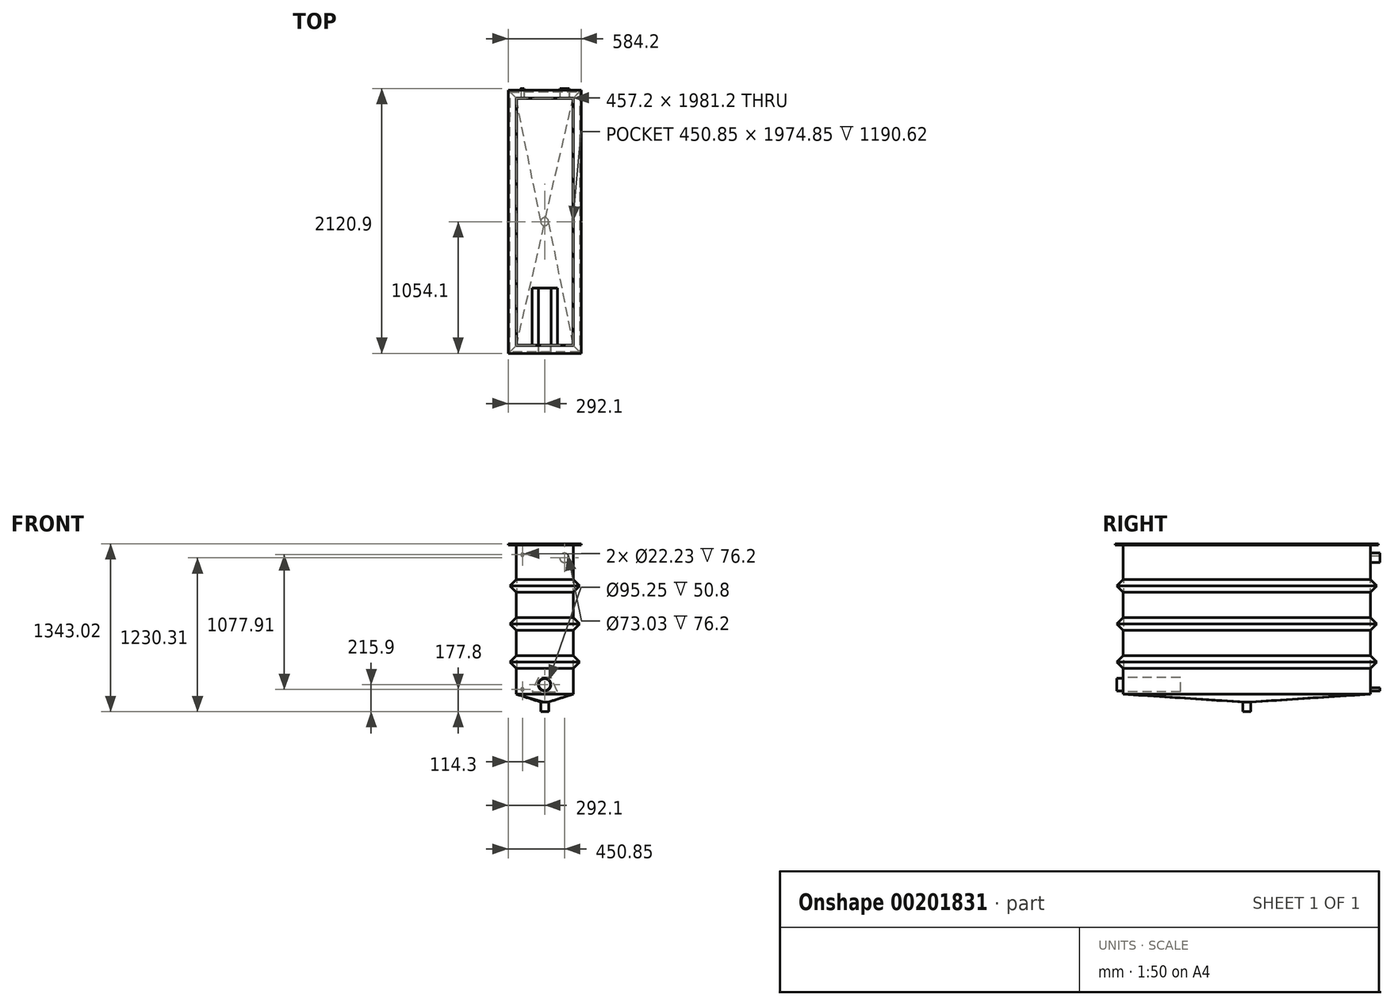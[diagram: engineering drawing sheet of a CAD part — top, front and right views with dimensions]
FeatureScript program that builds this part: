
annotation { "Feature Type Name" : "Feature", "Feature Type Description" : "" }
export const myFeature = defineFeature(function(context is Context, id is Id, definition is map)
    precondition{}
    {
        {
            var Q0;
            Q0=qCreatedBy(makeId("Right.planeOp"),FACE);
            var sketch = newSketch(context, id + "F0", { "sketchPlane" : qUnion([Q0])});
            skLineSegment(sketch, "E0.bottom", {"start": v(-990.6, 596.9) * mm, "end": v(990.6, 596.9) * mm});
            skLineSegment(sketch, "E0.top", {"start": v(-990.6, -596.9) * mm, "end": v(990.6, -596.9) * mm});
            skLineSegment(sketch, "E0.left", {"start": v(-990.6, 596.9) * mm, "end": v(-990.6, -596.9) * mm});
            skLineSegment(sketch, "E0.right", {"start": v(990.6, 596.9) * mm, "end": v(990.6, -596.9) * mm});
            skSolve(sketch);
        }
        {
            var Q0;
            Q0=makeQuery(id+"F0.imprint","IMPRINT",FACE,{"disambiguationData":[TD([[makeQuery(id+"F0.imprint","IMPRINT",EDGE,{"derivedFrom":sQuery(id+"F0.wireOp",EDGE,"E0.bottom")}),-1.0]])]});
            extrude(context, id + "F1", {"entities" : qUnion([Q0]), "endBound" : BoundingType.SYMMETRIC, "depth" : 457.2 * mm, "hasSecondDirection" : true, "secondDirectionOppositeDirection" : true, "secondDirectionDepth" : 228.6 * mm});
        }
        {
            var Q0;
            Q0=makeQuery(id+"F1.opExtrude","SWEPT_FACE",FACE,{"disambiguationData":[OSD([sQuery(id+"F0.wireOp",EDGE,"E0.bottom")])]});
            shell(context, id + "F2", {"entities" : qUnion([Q0]), "thickness" : 3.17 * mm});
        }
        {
            var Q0;
            Q0=makeQuery(id+"F1.opExtrude","SWEPT_FACE",FACE,{"disambiguationData":[OSD([sQuery(id+"F0.wireOp",EDGE,"E0.left")])]});
            var sketch = newSketch(context, id + "F3", { "sketchPlane" : qUnion([Q0])});
            skCircle(sketch, "E1", {"center": v(0, -520.7) * mm, "radius": 50.8 * mm});
            skCircle(sketch, "E2", {"center": v(0, -520.7) * mm, "radius": 47.63 * mm});
            skLineSegment(sketch, "E3", {"start": v(-571.69, -393.7) * mm, "end": v(666.68, -393.7) * mm, "construction": true});
            skSolve(sketch);
        }
        {
            var Q0;
            Q0=qSketchRegion(id+"F3",true);
            extrude(context, id + "F4", {"entities" : qUnion([Q0]), "depth" : 50.8 * mm});
        }
        {
            var Q0;
            Q0=makeQuery(id+"F2.opShell","OFFSET_FACE",FACE,{"disambiguationData":[OSD([sQuery(id+"F0.wireOp",EDGE,"E0.left")])]});
            var sketch = newSketch(context, id + "F5", { "sketchPlane" : qUnion([Q0])});
            skPoint(sketch, "E4", {"position": v(0, -520.7) * mm});
            skCircle(sketch, "E5", {"center": v(0, -520.7) * mm, "radius": 38.1 * mm, "construction": true});
            skLineSegment(sketch, "E6", {"start": v(-101.6, -577.85) * mm, "end": v(-50.8, -463.55) * mm});
            skLineSegment(sketch, "E7", {"start": v(-50.8, -463.55) * mm, "end": v(50.8, -463.55) * mm});
            skLineSegment(sketch, "E8", {"start": v(50.8, -463.55) * mm, "end": v(101.6, -577.85) * mm});
            skLineSegment(sketch, "E9", {"start": v(101.6, -577.85) * mm, "end": v(-101.6, -577.85) * mm});
            skSolve(sketch);
        }
        {
            var Q0;
            Q0=makeQuery(id+"F5.imprint","IMPRINT",FACE,{"disambiguationData":[TD([[makeQuery(id+"F5.imprint","IMPRINT",EDGE,{"derivedFrom":sQuery(id+"F5.wireOp",EDGE,"E6")}),-1.0]])]});
            extrude(context, id + "F6", {"entities" : qUnion([Q0]), "operationType" : NewBodyOperationType.ADD, "depth" : 457.2 * mm});
        }
        {
            var Q0;
            {var subQ1=sQuery(id+"F0.wireOp",EDGE,"E0.right");var subQ3=sQuery(id+"F0.wireOp",EDGE,"E0.bottom");Q0=makeQuery(id+"FLVfAFfTKYoEC7O_3.boolean.opBoolean","SPLIT",FACE,{"disambiguationData":[TD([makeQuery(id+"F1.opExtrude","SWEPT_FACE",FACE,{"disambiguationData":[OSD([subQ3])]})])],"derivedFrom":makeQuery(id+"F1.opExtrude","SWEPT_FACE",FACE,{"disambiguationData":[OSD([subQ1])]})});}
            var sketch = newSketch(context, id + "F7", { "sketchPlane" : qUnion([Q0])});
            skPoint(sketch, "E10", {"position": v(-158.75, 493.71) * mm});
            skCircle(sketch, "E11", {"center": v(-158.75, 493.71) * mm, "radius": 38.1 * mm});
            skCircle(sketch, "E12", {"center": v(-158.75, 493.71) * mm, "radius": 36.51 * mm});
            skPoint(sketch, "E13", {"position": v(-158.75, 457.2) * mm});
            skCircle(sketch, "E14", {"center": v(177.8, 519.11) * mm, "radius": 12.7 * mm});
            skCircle(sketch, "E15", {"center": v(177.8, 519.11) * mm, "radius": 11.11 * mm});
            skCircle(sketch, "E16", {"center": v(177.8, -558.8) * mm, "radius": 12.7 * mm});
            skCircle(sketch, "E17", {"center": v(177.8, -558.8) * mm, "radius": 11.11 * mm});
            skLineSegment(sketch, "E18", {"start": v(-180.53, -571.5) * mm, "end": v(332.18, -571.5) * mm, "construction": true});
            skLineSegment(sketch, "E19", {"start": v(-158.75, 493.71) * mm, "end": v(-158.75, 368.33) * mm, "construction": true});
            skPoint(sketch, "E20", {"position": v(-228.6, -381) * mm});
            skLineSegment(sketch, "E21", {"start": v(-172.42, 531.81) * mm, "end": v(289.09, 531.81) * mm, "construction": true});
            skSolve(sketch);
        }
        {
            var Q0;
            Q0=qSketchRegion(id+"F7",true);
            extrude(context, id + "F8", {"entities" : qUnion([Q0]), "operationType" : NewBodyOperationType.ADD, "depth" : 76.2 * mm});
        }
        {
            var Q0;
            Q0=makeQuery(id+"F2.opShell","OFFSET_FACE",FACE,{"disambiguationData":[OSD([sQuery(id+"F0.wireOp",EDGE,"E0.top")])]});
            cPlane(context, id + "F9", {"entities" : qUnion([Q0]), "cplaneType" : CPlaneType.OFFSET, "offset" : 254 * mm, "width" : 152.4 * mm, "height" : 152.4 * mm});
        }
        {
            var Q0;
            Q0=qCreatedBy(id+"F9.planeOp",FACE);
            var sketch = newSketch(context, id + "F10", { "sketchPlane" : qUnion([Q0])});
            skPoint(sketch, "E22", {"position": v(-225.43, 987.43) * mm});
            skPoint(sketch, "E23", {"position": v(228.6, 990.6) * mm});
            skPoint(sketch, "E24", {"position": v(228.6, -990.6) * mm});
            skPoint(sketch, "E25", {"position": v(-228.6, -990.6) * mm});
            skLineSegment(sketch, "E26", {"start": v(-228.6, -990.6) * mm, "end": v(-225.42, 987.43) * mm});
            skLineSegment(sketch, "E27", {"start": v(228.6, 990.6) * mm, "end": v(228.6, -990.6) * mm});
            skLineSegment(sketch, "E28", {"start": v(-225.42, 987.43) * mm, "end": v(228.6, 990.6) * mm});
            skLineSegment(sketch, "E29", {"start": v(-228.6, -990.6) * mm, "end": v(228.6, -990.6) * mm});
            skSolve(sketch);
        }
        {
            var Q0;
            Q0=makeQuery(id+"F1.opExtrude","SWEPT_FACE",FACE,{"disambiguationData":[OSD([sQuery(id+"F0.wireOp",EDGE,"E0.left")])]});
            var sketch = newSketch(context, id + "F11", { "sketchPlane" : qUnion([Q0])});
            skLineSegment(sketch, "E30", {"start": v(-228.6, -339.72) * mm, "end": v(-228.6, -390.52) * mm});
            skLineSegment(sketch, "E31", {"start": v(-228.6, -390.52) * mm, "end": v(-279.4, -339.72) * mm});
            skLineSegment(sketch, "E32", {"start": v(-279.4, -339.72) * mm, "end": v(-228.6, -288.92) * mm});
            skLineSegment(sketch, "E33", {"start": v(-228.6, -288.92) * mm, "end": v(-228.6, -339.72) * mm});
            skSolve(sketch);
        }
        {
            var Q0;
            Q0=makeQuery(id+"F11.imprint","IMPRINT",FACE,{"disambiguationData":[TD([[makeQuery(id+"F11.imprint","IMPRINT",EDGE,{"derivedFrom":sQuery(id+"F11.wireOp",EDGE,"E30")}),-1.0]])]});
            var Q1;
            Q1=sQuery(id+"F10.wireOp",EDGE,"E26");
            var Q2;
            Q2=sQuery(id+"F10.wireOp",EDGE,"E28");
            var Q3;
            Q3=sQuery(id+"F10.wireOp",EDGE,"E27");
            var Q4;
            Q4=sQuery(id+"F10.wireOp",EDGE,"E29");
            sweep(context, id + "F12", {"operationType" : NewBodyOperationType.ADD, "profiles" : qUnion([Q0]), "path" : qUnion([Q1, Q2, Q3, Q4])});
        }
        {
            var Q0;
            Q0=qCreatedBy(id+"F9.planeOp",FACE);
            cPlane(context, id + "F13", {"entities" : qUnion([Q0]), "cplaneType" : CPlaneType.OFFSET, "offset" : 304.8 * mm, "width" : 152.4 * mm, "height" : 152.4 * mm});
        }
        {
            var Q0;
            Q0=qCreatedBy(id+"F13.planeOp",FACE);
            var sketch = newSketch(context, id + "F14", { "sketchPlane" : qUnion([Q0])});
            skPoint(sketch, "E34", {"position": v(-228.6, 990.6) * mm});
            skPoint(sketch, "E35", {"position": v(228.6, 990.6) * mm});
            skPoint(sketch, "E36", {"position": v(228.6, -990.6) * mm});
            skPoint(sketch, "E37", {"position": v(-228.6, -990.6) * mm});
            skLineSegment(sketch, "E38", {"start": v(-228.6, -990.6) * mm, "end": v(-228.6, 990.6) * mm});
            skLineSegment(sketch, "E39", {"start": v(-228.6, 990.6) * mm, "end": v(228.6, 990.6) * mm});
            skLineSegment(sketch, "E40", {"start": v(228.6, 990.6) * mm, "end": v(228.6, -990.6) * mm});
            skLineSegment(sketch, "E41", {"start": v(228.6, -990.6) * mm, "end": v(-228.6, -990.6) * mm});
            skSolve(sketch);
        }
        {
            var Q0;
            {var subQ1=sQuery(id+"F0.wireOp",EDGE,"E0.left");var subQ3=sQuery(id+"F0.wireOp",EDGE,"E0.bottom");Q0=makeQuery(id+"F12.boolean.opBoolean","SPLIT",FACE,{"disambiguationData":[TD([makeQuery(id+"F1.opExtrude","SWEPT_FACE",FACE,{"disambiguationData":[OSD([subQ3])]})])],"derivedFrom":makeQuery(id+"F1.opExtrude","SWEPT_FACE",FACE,{"disambiguationData":[OSD([subQ1])]})});}
            var sketch = newSketch(context, id + "F15", { "sketchPlane" : qUnion([Q0])});
            skPoint(sketch, "E42", {"position": v(-228.6, -34.92) * mm});
            skLineSegment(sketch, "E43", {"start": v(-228.6, -34.92) * mm, "end": v(-228.6, -85.72) * mm});
            skLineSegment(sketch, "E44", {"start": v(-228.6, -85.72) * mm, "end": v(-279.4, -34.92) * mm});
            skLineSegment(sketch, "E45", {"start": v(-279.4, -34.92) * mm, "end": v(-228.6, 15.88) * mm});
            skLineSegment(sketch, "E46", {"start": v(-228.6, 15.88) * mm, "end": v(-228.6, -34.92) * mm});
            skSolve(sketch);
        }
        {
            var Q0;
            Q0=qCreatedBy(id+"F13.planeOp",FACE);
            cPlane(context, id + "F16", {"entities" : qUnion([Q0]), "cplaneType" : CPlaneType.OFFSET, "offset" : 304.8 * mm, "width" : 152.4 * mm, "height" : 152.4 * mm});
        }
        {
            var Q0;
            Q0=qCreatedBy(id+"F16.planeOp",FACE);
            var sketch = newSketch(context, id + "F17", { "sketchPlane" : qUnion([Q0])});
            skPoint(sketch, "E47", {"position": v(-228.6, 990.6) * mm});
            skPoint(sketch, "E48", {"position": v(228.6, 990.6) * mm});
            skPoint(sketch, "E49", {"position": v(228.6, -990.6) * mm});
            skPoint(sketch, "E50", {"position": v(-228.6, -990.6) * mm});
            skLineSegment(sketch, "E51", {"start": v(-228.6, -990.6) * mm, "end": v(-228.6, 990.6) * mm});
            skLineSegment(sketch, "E52", {"start": v(-228.6, 990.6) * mm, "end": v(228.6, 990.6) * mm});
            skLineSegment(sketch, "E53", {"start": v(228.6, 990.6) * mm, "end": v(228.6, -990.6) * mm});
            skLineSegment(sketch, "E54", {"start": v(228.6, -990.6) * mm, "end": v(-228.6, -990.6) * mm});
            skSolve(sketch);
        }
        {
            var Q0;
            {var subQ2=sQuery(id+"F0.wireOp",EDGE,"E0.left");var subQ4=sQuery(id+"F0.wireOp",EDGE,"E0.bottom");var subQ7=makeQuery(id+"F1.opExtrude","SWEPT_FACE",FACE,{"disambiguationData":[OSD([subQ4])]});Q0=makeQuery(id+"FEdXTNuG9fACU3v_4.boolean.opBoolean","SPLIT",FACE,{"disambiguationData":[TD([subQ7])],"derivedFrom":makeQuery(id+"F12.boolean.opBoolean","SPLIT",FACE,{"disambiguationData":[TD([subQ7])],"derivedFrom":makeQuery(id+"F1.opExtrude","SWEPT_FACE",FACE,{"disambiguationData":[OSD([subQ2])]})})});}
            var sketch = newSketch(context, id + "F18", { "sketchPlane" : qUnion([Q0])});
            skPoint(sketch, "E55", {"position": v(-228.6, 269.88) * mm});
            skLineSegment(sketch, "E56", {"start": v(-228.6, 269.88) * mm, "end": v(-228.6, 219.08) * mm});
            skLineSegment(sketch, "E57", {"start": v(-228.6, 219.08) * mm, "end": v(-279.4, 269.88) * mm});
            skLineSegment(sketch, "E58", {"start": v(-279.4, 269.88) * mm, "end": v(-228.6, 320.68) * mm});
            skLineSegment(sketch, "E59", {"start": v(-228.6, 320.68) * mm, "end": v(-228.6, 269.88) * mm});
            skSolve(sketch);
        }
        {
            var Q0;
            Q0=makeQuery(id+"F18.imprint","IMPRINT",FACE,{"disambiguationData":[TD([[makeQuery(id+"F18.imprint","IMPRINT",EDGE,{"derivedFrom":sQuery(id+"F18.wireOp",EDGE,"E56")}),-1.0]])]});
            var Q1;
            Q1=sQuery(id+"F17.wireOp",EDGE,"E51");
            var Q2;
            Q2=sQuery(id+"F17.wireOp",EDGE,"E52");
            var Q3;
            Q3=sQuery(id+"F17.wireOp",EDGE,"E53");
            var Q4;
            Q4=sQuery(id+"F17.wireOp",EDGE,"E54");
            sweep(context, id + "F19", {"operationType" : NewBodyOperationType.ADD, "profiles" : qUnion([Q0]), "path" : qUnion([Q1, Q2, Q3, Q4])});
        }
        {
            var Q0;
            Q0=makeQuery(id+"F1.opExtrude","SWEPT_FACE",FACE,{"disambiguationData":[OSD([sQuery(id+"F0.wireOp",EDGE,"E0.bottom")])]});
            var sketch = newSketch(context, id + "F20", { "sketchPlane" : qUnion([Q0])});
            skPoint(sketch, "E60", {"position": v(-292.1, 1054.1) * mm});
            skPoint(sketch, "E61", {"position": v(292.1, -1054.1) * mm});
            skLineSegment(sketch, "E62.bottom", {"start": v(-225.43, 987.43) * mm, "end": v(225.42, 987.43) * mm});
            skLineSegment(sketch, "E62.top", {"start": v(-225.42, -987.43) * mm, "end": v(225.43, -987.43) * mm});
            skLineSegment(sketch, "E62.left", {"start": v(-225.43, 987.43) * mm, "end": v(-225.42, -987.43) * mm});
            skLineSegment(sketch, "E62.right", {"start": v(225.42, 987.43) * mm, "end": v(225.43, -987.43) * mm});
            skLineSegment(sketch, "E63.bottom", {"start": v(-292.1, 1054.1) * mm, "end": v(292.1, 1054.1) * mm});
            skLineSegment(sketch, "E63.top", {"start": v(-292.1, -1054.1) * mm, "end": v(292.1, -1054.1) * mm});
            skLineSegment(sketch, "E63.left", {"start": v(-292.1, 1054.1) * mm, "end": v(-292.1, -1054.1) * mm});
            skLineSegment(sketch, "E63.right", {"start": v(292.1, 1054.1) * mm, "end": v(292.1, -1054.1) * mm});
            skSolve(sketch);
        }
        {
            var Q0;
            Q0=makeQuery(id+"F15.imprint","IMPRINT",FACE,{"disambiguationData":[TD([[makeQuery(id+"F15.imprint","IMPRINT",EDGE,{"derivedFrom":sQuery(id+"F15.wireOp",EDGE,"E43")}),-1.0]])]});
            var Q1;
            Q1=sQuery(id+"F14.wireOp",EDGE,"E38");
            var Q2;
            Q2=sQuery(id+"F14.wireOp",EDGE,"E39");
            var Q3;
            Q3=sQuery(id+"F14.wireOp",EDGE,"E40");
            var Q4;
            Q4=sQuery(id+"F14.wireOp",EDGE,"E41");
            sweep(context, id + "F21", {"operationType" : NewBodyOperationType.ADD, "profiles" : qUnion([Q0]), "path" : qUnion([Q1, Q2, Q3, Q4])});
        }
        {
            var Q0;
            Q0=makeQuery(id+"F20.imprint","IMPRINT",FACE,{"disambiguationData":[TD([[makeQuery(id+"F20.imprint","IMPRINT",EDGE,{"derivedFrom":sQuery(id+"F20.wireOp",EDGE,"E63.bottom")}),-1.0]])]});
            extrude(context, id + "F22", {"entities" : qUnion([Q0]), "depth" : 9.52 * mm});
        }
        {
            var Q0;
            Q0=makeQuery(id+"F1.opExtrude","SWEPT_FACE",FACE,{"disambiguationData":[OSD([sQuery(id+"F0.wireOp",EDGE,"E0.top")])]});
            cPlane(context, id + "F23", {"entities" : qUnion([Q0]), "cplaneType" : CPlaneType.OFFSET, "offset" : 63.5 * mm, "width" : 152.4 * mm, "height" : 152.4 * mm});
        }
        {
            var Q0;
            Q0=qCreatedBy(id+"F23.planeOp",FACE);
            var sketch = newSketch(context, id + "F24", { "sketchPlane" : qUnion([Q0])});
            skPoint(sketch, "E64.middle", {"position": v(0, 0) * mm});
            skCircle(sketch, "E65", {"center": v(0, 0) * mm, "radius": 31.75 * mm});
            skSolve(sketch);
        }
        {
            var Q1;
            Q1=makeQuery(id+"F24.imprint","IMPRINT",FACE,{"disambiguationData":[TD([[makeQuery(id+"F24.imprint","IMPRINT",EDGE,{"derivedFrom":sQuery(id+"F24.wireOp",EDGE,"E65")}),1.0]])]});
            var Q2;
            Q2=makeQuery(id+"F1.opExtrude","SWEPT_FACE",FACE,{"disambiguationData":[OSD([sQuery(id+"F0.wireOp",EDGE,"E0.top")])]});
            loft(context, id + "F25", {"operationType" : NewBodyOperationType.ADD, "sheetProfilesArray" : [{ "sheetProfileEntities" : qUnion([Q1]) }, { "sheetProfileEntities" : qUnion([Q2]) }]});
        }
        {
            var Q0;
            Q0=makeQuery(id+"F25.opLoft","CAP_FACE",FACE,{"disambiguationData":[OSD([makeQuery(id+"F24.imprint","IMPRINT",FACE,{"disambiguationData":[TD([[makeQuery(id+"F24.imprint","IMPRINT",EDGE,{"derivedFrom":sQuery(id+"F24.wireOp",EDGE,"E65")}),1.0]])]})])],"isStart":true});
            extrude(context, id + "F26", {"entities" : qUnion([Q0]), "operationType" : NewBodyOperationType.ADD, "depth" : 76.2 * mm});
        }
    });
